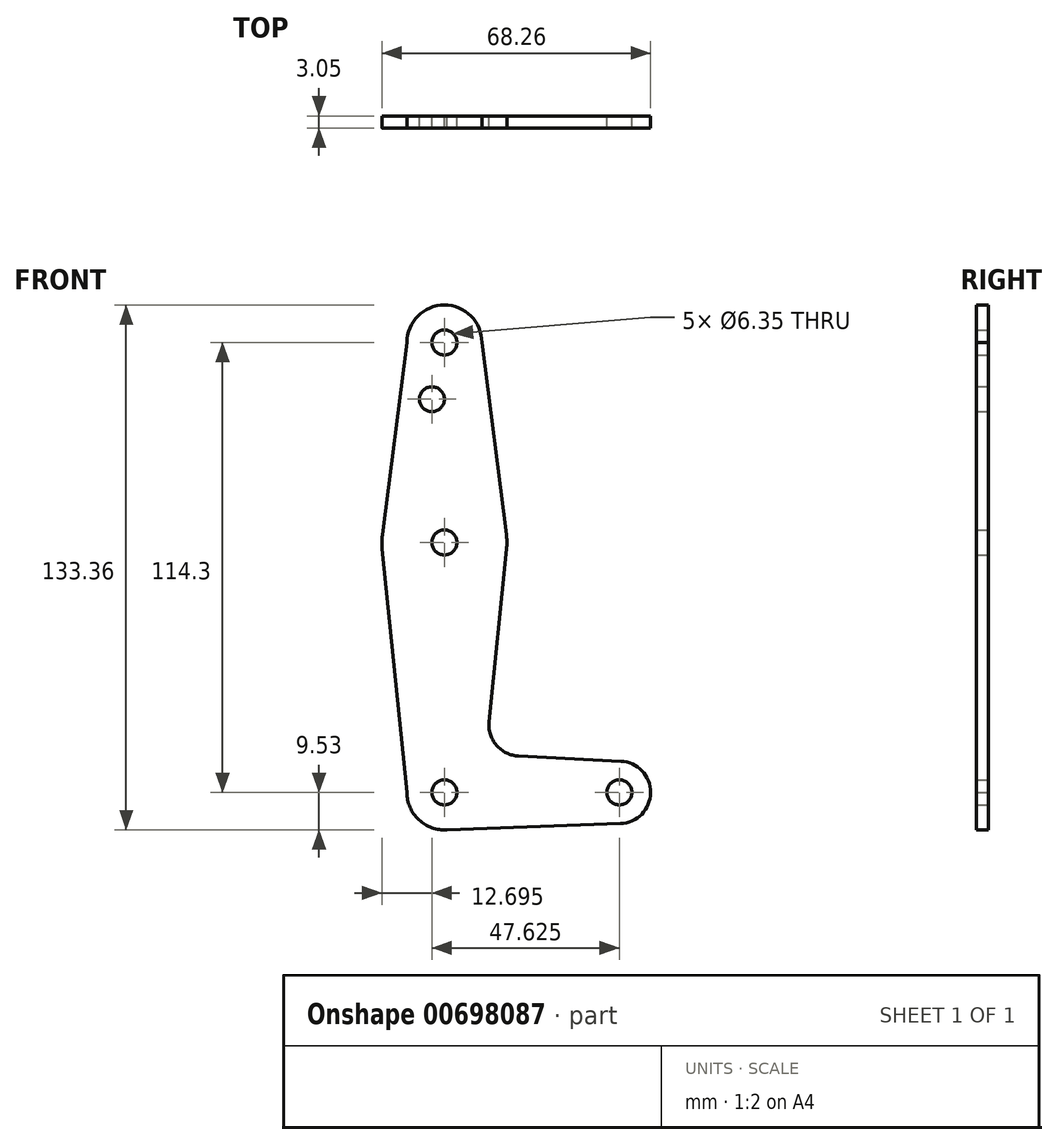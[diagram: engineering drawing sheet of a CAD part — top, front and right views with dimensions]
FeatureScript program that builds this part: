
annotation { "Feature Type Name" : "Feature", "Feature Type Description" : "" }
export const myFeature = defineFeature(function(context is Context, id is Id, definition is map)
    precondition{}
    {
        {
            var Q0;
            Q0=qCreatedBy(makeId("Front.planeOp"),FACE);
            var sketch = newSketch(context, id + "F0", { "sketchPlane" : qUnion([Q0])});
            skCircle(sketch, "E0", {"center": v(0, 0) * mm, "radius": 9.53 * mm});
            skCircle(sketch, "E1", {"center": v(0, 63.5) * mm, "radius": 15.88 * mm});
            skCircle(sketch, "E2", {"center": v(0, 114.3) * mm, "radius": 9.53 * mm});
            skCircle(sketch, "E3", {"center": v(44.45, 0) * mm, "radius": 7.94 * mm});
            skLineSegment(sketch, "E4", {"start": v(0, 114.3) * mm, "end": v(0, 63.5) * mm, "construction": true});
            skLineSegment(sketch, "E5", {"start": v(0, 63.5) * mm, "end": v(0, 0) * mm, "construction": true});
            skLineSegment(sketch, "E6", {"start": v(44.45, 0) * mm, "end": v(0, 0) * mm, "construction": true});
            skLineSegment(sketch, "E7", {"start": v(-9.53, 114.3) * mm, "end": v(-15.75, 65.5) * mm});
            skLineSegment(sketch, "E8", {"start": v(11.34, 17.96) * mm, "end": v(15.8, 61.9) * mm});
            skLineSegment(sketch, "E9", {"start": v(18.86, 9.22) * mm, "end": v(44.84, 7.93) * mm});
            skLineSegment(sketch, "E10", {"start": v(0, -9.53) * mm, "end": v(44.73, -7.93) * mm});
            skLineSegment(sketch, "E11", {"start": v(9.52, 114.3) * mm, "end": v(15.75, 65.5) * mm});
            skArc(sketch, "E12.filletArc", {"start": v(11.34, 17.96) * mm, "mid": v(13.23, 11.98) * mm, "end": v(18.86, 9.22) * mm});
            skCircle(sketch, "E13", {"center": v(0, 114.3) * mm, "radius": 3.18 * mm});
            skCircle(sketch, "E14", {"center": v(0, 63.5) * mm, "radius": 3.17 * mm});
            skCircle(sketch, "E15", {"center": v(0, 0) * mm, "radius": 3.18 * mm});
            skCircle(sketch, "E16", {"center": v(44.45, 0) * mm, "radius": 3.18 * mm});
            skCircle(sketch, "E17", {"center": v(-3.17, 99.89) * mm, "radius": 3.18 * mm});
            skLineSegment(sketch, "E18", {"start": v(-9.53, 0) * mm, "end": v(-15.8, 61.9) * mm});
            skSolve(sketch);
        }
        {
            var Q0;
            Q0 = qSketchRegion(id + "F0", true);
            extrude(context, id + "F1", {"entities" : qUnion([Q0]), "depth" : 3.05 * mm, "offsetDistance" : 25.4 * mm});
        }
    });
